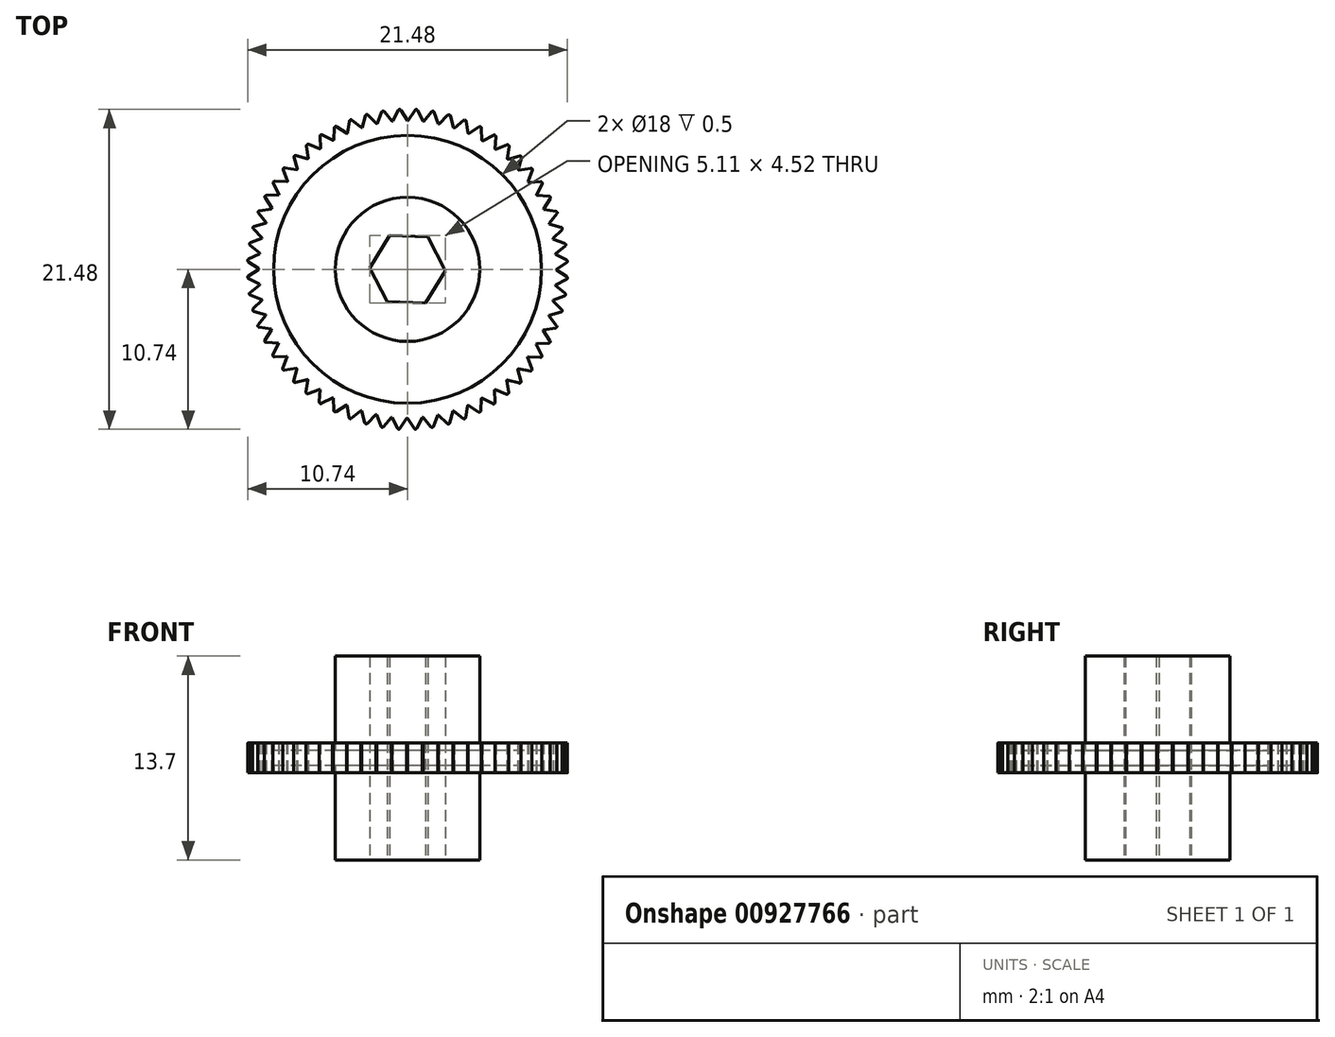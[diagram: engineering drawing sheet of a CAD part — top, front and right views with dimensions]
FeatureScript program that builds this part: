
annotation { "Feature Type Name" : "Feature", "Feature Type Description" : "" }
export const myFeature = defineFeature(function(context is Context, id is Id, definition is map)
    precondition{}
    {
        {
            var Q0;
            Q0=qCreatedBy(makeId("Top.planeOp"),FACE);
            var sketch = newSketch(context, id + "F0", { "sketchPlane" : qUnion([Q0])});
            skCircle(sketch, "E0", {"center": v(0, 0) * mm, "radius": 4.85 * mm});
            skArc(sketch, "E1", {"start": v(-1, 9.95) * mm, "mid": v(0.5, -9.99) * mm, "end": v(0, 10) * mm});
            skCircle(sketch, "E2", {"center": v(0, 0) * mm, "radius": 9 * mm});
            skLineSegment(sketch, "E3", {"start": v(-1, 9.95) * mm, "end": v(0, 10) * mm});
            skLineSegment(sketch, "E4", {"start": v(-1, 9.95) * mm, "end": v(-0.62, 10.69) * mm});
            skLineSegment(sketch, "E5", {"start": v(-0.45, 10.7) * mm, "end": v(0, 10) * mm});
            skPoint(sketch, "E6.visualSharp", {"position": v(-0.54, 10.84) * mm});
            skArc(sketch, "E6.filletArc", {"start": v(-0.45, 10.7) * mm, "mid": v(-0.54, 10.74) * mm, "end": v(-0.62, 10.69) * mm});
            skPoint(sketch, "E7.0.midPoint", {"position": v(-1.32, 0.78) * mm});
            skPoint(sketch, "E8.0.midPoint", {"position": v(-1.7, 1.07) * mm});
            skPoint(sketch, "E9.orphan", {"position": v(-0.9, -1.52) * mm});
            skPoint(sketch, "E10.orphan", {"position": v(0.87, -1.54) * mm});
            skPoint(sketch, "E11.orphan", {"position": v(-1.77, 0.02) * mm});
            skPoint(sketch, "E7.1.start.orphan", {"position": v(-0.87, 1.54) * mm});
            skArc(sketch, "E12.cCircle", {"start": v(0.99, 1.98) * mm, "mid": v(-1.55, -1.59) * mm, "end": v(1.96, 1.04) * mm, "construction": true});
            skLineSegment(sketch, "E12.0", {"start": v(1.36, 2.17) * mm, "end": v(2.56, -0.1) * mm});
            skLineSegment(sketch, "E12.1", {"start": v(2.56, -0.1) * mm, "end": v(1.2, -2.26) * mm});
            skLineSegment(sketch, "E12.2", {"start": v(1.2, -2.26) * mm, "end": v(-1.36, -2.17) * mm});
            skLineSegment(sketch, "E12.3", {"start": v(-1.36, -2.17) * mm, "end": v(-2.56, 0.1) * mm});
            skLineSegment(sketch, "E12.4", {"start": v(-2.56, 0.1) * mm, "end": v(-1.2, 2.26) * mm});
            skLineSegment(sketch, "E12.5", {"start": v(-1.2, 2.26) * mm, "end": v(1.36, 2.17) * mm});
            skPoint(sketch, "E12.0.midPoint", {"position": v(1.96, 1.04) * mm});
            skPoint(sketch, "E8.1.start.orphan", {"position": v(-1.1, 2.06) * mm});
            skPoint(sketch, "E13.orphan", {"position": v(1.1, -2.06) * mm});
            skPoint(sketch, "E14.orphan", {"position": v(-1.24, -1.97) * mm});
            skPoint(sketch, "E8.5.end.orphan", {"position": v(-2.33, 0.08) * mm});
            skSolve(sketch);
        }
        {
            var Q0;
            Q0=qCreatedBy(makeId("Front.planeOp"),FACE);
            var sketch = newSketch(context, id + "F1", { "sketchPlane" : qUnion([Q0])});
            skLineSegment(sketch, "E15", {"start": v(0, 0) * mm, "end": v(0, 26.77) * mm, "construction": true});
            skSolve(sketch);
        }
        {
            var Q0;
            Q0=makeQuery(id+"F0.imprint","IMPRINT",FACE,{"disambiguationData":[TD([[makeQuery(id+"F0.imprint","IMPRINT",EDGE,{"derivedFrom":sQuery(id+"F0.wireOp",EDGE,"E0")}),1.0]])]});
            extrude(context, id + "F2", {"entities" : qUnion([Q0]), "endBound" : BoundingType.SYMMETRIC, "depth" : 13.7 * mm, "offsetDistance" : 25 * mm});
        }
        {
            var Q0;
            Q0=makeQuery(id+"F0.imprint","IMPRINT",FACE,{"disambiguationData":[TD([[makeQuery(id+"F0.imprint","IMPRINT",EDGE,{"derivedFrom":sQuery(id+"F0.wireOp",EDGE,"E0")}),-1.0]])]});
            extrude(context, id + "F3", {"entities" : qUnion([Q0]), "operationType" : NewBodyOperationType.ADD, "endBound" : BoundingType.SYMMETRIC, "depth" : 1 * mm, "offsetDistance" : 25 * mm});
        }
        {
            var Q0;
            Q0=makeQuery(id+"F0.imprint","IMPRINT",FACE,{"disambiguationData":[TD([[makeQuery(id+"F0.imprint","IMPRINT",EDGE,{"derivedFrom":sQuery(id+"F0.wireOp",EDGE,"E2")}),-1.0]])]});
            extrude(context, id + "F4", {"entities" : qUnion([Q0]), "operationType" : NewBodyOperationType.ADD, "endBound" : BoundingType.SYMMETRIC, "depth" : 2 * mm, "offsetDistance" : 25 * mm});
        }
        {
            var Q0;
            {var subQ5=sQuery(id+"F0.wireOp",EDGE,"E4");Q0=makeQuery(id+"F0.imprint","IMPRINT",FACE,{"disambiguationData":[TD([[makeQuery(id+"F0.imprint","IMPRINT",EDGE,{"derivedFrom":subQ5}),-1.0]])]});}
            extrude(context, id + "F5", {"entities" : qUnion([Q0]), "endBound" : BoundingType.SYMMETRIC, "depth" : 2 * mm, "offsetDistance" : 25 * mm});
        }
        {
            var Q0;
            Q0=makeQuery(id+"F5.opExtrude","SWEPT_BODY",BODY,{"disambiguationData":[OSD([sQuery(id+"F0.wireOp",EDGE,"E3"),sQuery(id+"F0.wireOp",EDGE,"E4"),sQuery(id+"F0.wireOp",EDGE,"E5")])]});
            var Q1;
            Q1=sQuery(id+"F1.wireOp",EDGE,"E15");
            circularPattern(context, id + "F6", {"operationType" : NewBodyOperationType.ADD, "entities" : qUnion([Q0]), "axis" : qUnion([Q1]), "angle" : 360 * degree, "instanceCount" : 60, "equalSpace" : true});
        }
    });
